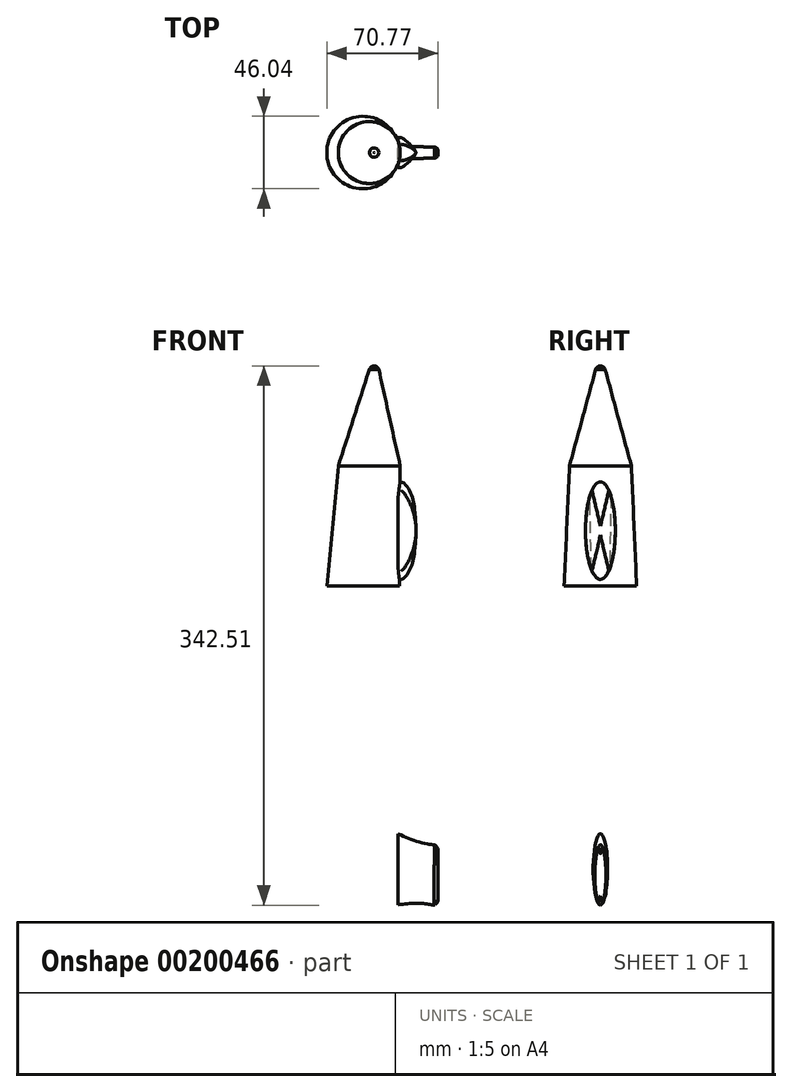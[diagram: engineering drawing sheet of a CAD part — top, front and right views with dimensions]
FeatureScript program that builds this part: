
annotation { "Feature Type Name" : "Feature", "Feature Type Description" : "" }
export const myFeature = defineFeature(function(context is Context, id is Id, definition is map)
    precondition{}
    {
        {
            var Q0;
            Q0=qCreatedBy(makeId("Top.planeOp"),FACE);
            var sketch = newSketch(context, id + "F0", { "sketchPlane" : qUnion([Q0])});
            skCircle(sketch, "E0", {"center": v(0, 0) * mm, "radius": 23.24 * mm});
            skSolve(sketch);
        }
        {
            var Q0;
            Q0=makeQuery(id+"F0.imprint","IMPRINT",FACE,{"disambiguationData":[TD([[makeQuery(id+"F0.imprint","IMPRINT",EDGE,{"derivedFrom":sQuery(id+"F0.wireOp",EDGE,"E0")}),1.0]])]});
            extrude(context, id + "F1", {"entities" : qUnion([Q0]), "depth" : 76.2 * mm, "hasSecondDirection" : true, "secondDirectionOppositeDirection" : true, "secondDirectionDepth" : 127 * mm});
        }
        {
            var Q0;
            Q0=makeQuery(id+"F1.opExtrude","CAP_FACE",FACE,{"disambiguationData":[OSD([sQuery(id+"F0.wireOp",EDGE,"E0")])],"isStart":false});
            var sketch = newSketch(context, id + "F2", { "sketchPlane" : qUnion([Q0])});
            skCircle(sketch, "E1", {"center": v(0, 0) * mm, "radius": 23.02 * mm});
            skSolve(sketch);
        }
        {
            var Q0;
            Q0=makeQuery(id+"F2.imprint","IMPRINT",FACE,{"disambiguationData":[TD([[makeQuery(id+"F2.imprint","IMPRINT",EDGE,{"derivedFrom":sQuery(id+"F2.wireOp",EDGE,"E1")}),1.0]])]});
            cPlane(context, id + "F3", {"entities" : qUnion([Q0]), "cplaneType" : CPlaneType.OFFSET, "offset" : 76.2 * mm, "width" : 152.4 * mm, "height" : 152.4 * mm});
        }
        {
            var Q0;
            Q0=qCreatedBy(id+"F3.planeOp",FACE);
            var sketch = newSketch(context, id + "F4", { "sketchPlane" : qUnion([Q0])});
            skCircle(sketch, "E2", {"center": v(3.96, 0) * mm, "radius": 19.65 * mm});
            skSolve(sketch);
        }
        {
            var Q1;
            Q1=makeQuery(id+"F2.imprint","IMPRINT",FACE,{"disambiguationData":[TD([[makeQuery(id+"F2.imprint","IMPRINT",EDGE,{"derivedFrom":sQuery(id+"F2.wireOp",EDGE,"E1")}),1.0]])]});
            var Q2;
            Q2=makeQuery(id+"F4.imprint","IMPRINT",FACE,{"disambiguationData":[TD([[makeQuery(id+"F4.imprint","IMPRINT",EDGE,{"derivedFrom":sQuery(id+"F4.wireOp",EDGE,"E2")}),1.0]])]});
            loft(context, id + "F5", {"sheetProfilesArray" : [{ "sheetProfileEntities" : qUnion([Q1]) }, { "sheetProfileEntities" : qUnion([Q2]) }]});
        }
        {
            var Q0;
            Q0=qCreatedBy(makeId("Right.planeOp"),FACE);
            cPlane(context, id + "F6", {"entities" : qUnion([Q0]), "cplaneType" : CPlaneType.OFFSET, "offset" : 17.78 * mm, "width" : 152.4 * mm, "height" : 152.4 * mm});
        }
        {
            var Q0;
            Q0=qCreatedBy(makeId("Front.planeOp"),FACE);
            var sketch = newSketch(context, id + "F7", { "sketchPlane" : qUnion([Q0])});
            skEllipse(sketch, "E3", {"center": v(0, 0) * mm, "majorRadius": 116.9 * mm, "minorRadius": 9.43 * mm, "majorAxis": v(0, 1)});
            skSolve(sketch);
        }
        {
            var Q0;
            Q0=qCreatedBy(makeId("Front.planeOp"),FACE);
            cPlane(context, id + "F8", {"entities" : qUnion([Q0]), "cplaneType" : CPlaneType.OFFSET, "offset" : 88.9 * mm, "width" : 152.4 * mm, "height" : 152.4 * mm});
        }
        {
            var Q0;
            Q0=qCreatedBy(id+"F8.planeOp",FACE);
            var sketch = newSketch(context, id + "F9", { "sketchPlane" : qUnion([Q0])});
            skEllipse(sketch, "E4", {"center": v(0, -72.55) * mm, "majorRadius": 42.33 * mm, "minorRadius": 3.66 * mm, "majorAxis": v(0, 1)});
            skSolve(sketch);
        }
        {
            var Q0;
            Q0=makeQuery(id+"F7.imprint","IMPRINT",FACE,{"disambiguationData":[TD([[makeQuery(id+"F7.imprint","IMPRINT",EDGE,{"derivedFrom":sQuery(id+"F7.wireOp",EDGE,"E3")}),1.0]])]});
            var Q1;
            Q1=makeQuery(id+"F9.imprint","IMPRINT",FACE,{"disambiguationData":[TD([[makeQuery(id+"F9.imprint","IMPRINT",EDGE,{"derivedFrom":sQuery(id+"F9.wireOp",EDGE,"E4")}),1.0]])]});
            loft(context, id + "F10", {"bodyType" : ToolBodyType.SURFACE, "wireProfilesArray" : [{ "wireProfileEntities" : qUnion([Q0]) }, { "wireProfileEntities" : qUnion([Q1]) }]});
        }
        {
            var Q0;
            Q0=makeQuery(id+"F10.opLoft","SWEPT_BODY",BODY,{"disambiguationData":[OSD([sQuery(id+"F7.wireOp",EDGE,"E3"),sQuery(id+"F9.wireOp",EDGE,"E4")])]});
            var Q1;
            Q1=qCreatedBy(makeId("Front.planeOp"),FACE);
            mirror(context, id + "F11", {"entities" : qUnion([Q0]), "mirrorPlane" : qUnion([Q1])});
        }
        {
            var Q0;
            Q0=makeQuery(id+"F4.imprint","IMPRINT",FACE,{"disambiguationData":[TD([[makeQuery(id+"F4.imprint","IMPRINT",EDGE,{"derivedFrom":sQuery(id+"F4.wireOp",EDGE,"E2")}),1.0]])]});
            cPlane(context, id + "F12", {"entities" : qUnion([Q0]), "cplaneType" : CPlaneType.OFFSET, "offset" : 63.5 * mm, "width" : 152.4 * mm, "height" : 152.4 * mm});
        }
        {
            var Q0;
            Q0=qCreatedBy(id+"F12.planeOp",FACE);
            var sketch = newSketch(context, id + "F13", { "sketchPlane" : qUnion([Q0])});
            skCircle(sketch, "E5", {"center": v(7.13, 0) * mm, "radius": 2.4 * mm});
            skSolve(sketch);
        }
        {
            var Q0;
            Q0=makeQuery(id+"F13.imprint","IMPRINT",FACE,{"disambiguationData":[TD([[makeQuery(id+"F13.imprint","IMPRINT",EDGE,{"derivedFrom":sQuery(id+"F13.wireOp",EDGE,"E5")}),1.0]])]});
            var Q1;
            Q1=makeQuery(id+"F4.imprint","IMPRINT",FACE,{"disambiguationData":[TD([[makeQuery(id+"F4.imprint","IMPRINT",EDGE,{"derivedFrom":sQuery(id+"F4.wireOp",EDGE,"E2")}),1.0]])]});
            loft(context, id + "F14", {"sheetProfilesArray" : [{ "sheetProfileEntities" : qUnion([Q0]) }, { "sheetProfileEntities" : qUnion([Q1]) }]});
        }
        {
            var Q0;
            Q0=makeQuery(id+"F14.opLoft","CAP_FACE",FACE,{"disambiguationData":[OSD([makeQuery(id+"F13.imprint","IMPRINT",FACE,{"disambiguationData":[TD([[makeQuery(id+"F13.imprint","IMPRINT",EDGE,{"derivedFrom":sQuery(id+"F13.wireOp",EDGE,"E5")}),1.0]])]})])],"isStart":true});
            fillet(context, id + "F15", {"entities" : qUnion([Q0]), "radius" : 3.05 * mm, "tangentPropagation" : true, "allowEdgeOverflow" : false});
        }
        {
            var Q0;
            Q0=qCreatedBy(id+"F6.planeOp",FACE);
            cPlane(context, id + "F16", {"entities" : qUnion([Q0]), "cplaneType" : CPlaneType.OFFSET, "offset" : 4.57 * mm, "width" : 152.4 * mm, "height" : 152.4 * mm});
        }
        {
            var Q0;
            Q0=qCreatedBy(id+"F16.planeOp",FACE);
            var sketch = newSketch(context, id + "F17", { "sketchPlane" : qUnion([Q0])});
            skEllipse(sketch, "E6", {"center": v(0, 111.29) * mm, "majorRadius": 30.95 * mm, "minorRadius": 9.47 * mm, "majorAxis": v(0, 1)});
            skSolve(sketch);
        }
        {
            var Q0;
            Q0=makeQuery(id+"F17.imprint","IMPRINT",FACE,{"disambiguationData":[TD([[makeQuery(id+"F17.imprint","IMPRINT",EDGE,{"derivedFrom":sQuery(id+"F17.wireOp",EDGE,"E6")}),1.0]])]});
            extrude(context, id + "F18", {"entities" : qUnion([Q0]), "operationType" : NewBodyOperationType.ADD, "depth" : 11.18 * mm});
        }
        {
            var Q0;
            Q0=makeQuery(id+"F18.opExtrude","CAP_EDGE",EDGE,{"disambiguationData":[OSD([sQuery(id+"F17.wireOp",EDGE,"E6")])],"isStart":false});
            fillet(context, id + "F19", {"entities" : qUnion([Q0]), "radius" : 9.42 * mm, "tangentPropagation" : true, "rho" : .15, "crossSection" : FilletCrossSection.CONIC, "allowEdgeOverflow" : false});
        }
        {
            var Q0;
            Q0=qCreatedBy(id+"F16.planeOp",FACE);
            var sketch = newSketch(context, id + "F20", { "sketchPlane" : qUnion([Q0])});
            skEllipse(sketch, "E7", {"center": v(0, -103.87) * mm, "majorRadius": 22.62 * mm, "minorRadius": 4.6 * mm, "majorAxis": v(0, 1)});
            skSolve(sketch);
        }
        {
            var Q0;
            Q0=qCreatedBy(id+"F16.planeOp",FACE);
            cPlane(context, id + "F21", {"entities" : qUnion([Q0]), "cplaneType" : CPlaneType.OFFSET, "offset" : 25.4 * mm, "width" : 152.4 * mm, "height" : 152.4 * mm});
        }
        {
            var Q0;
            Q0=qCreatedBy(id+"F21.planeOp",FACE);
            var sketch = newSketch(context, id + "F22", { "sketchPlane" : qUnion([Q0])});
            skEllipse(sketch, "E8", {"center": v(0, -107.9) * mm, "majorRadius": 19.49 * mm, "minorRadius": 3.54 * mm, "majorAxis": v(0, 1)});
            skSolve(sketch);
        }
        {
            var Q0;
            Q0=makeQuery(id+"F22.imprint","IMPRINT",FACE,{"disambiguationData":[TD([[makeQuery(id+"F22.imprint","IMPRINT",EDGE,{"derivedFrom":sQuery(id+"F22.wireOp",EDGE,"E8")}),1.0]])]});
            var Q1;
            Q1=makeQuery(id+"F20.imprint","IMPRINT",FACE,{"disambiguationData":[TD([[makeQuery(id+"F20.imprint","IMPRINT",EDGE,{"derivedFrom":sQuery(id+"F20.wireOp",EDGE,"E7")}),1.0]])]});
            loft(context, id + "F23", {"sheetProfilesArray" : [{ "sheetProfileEntities" : qUnion([Q0]) }, { "sheetProfileEntities" : qUnion([Q1]) }]});
        }
        {
            var Q0;
            Q0=makeQuery(id+"F23.opLoft","MID_CAP_EDGE",EDGE,{"disambiguationData":[OSD([sQuery(id+"F22.wireOp",EDGE,"E8")])],"capPos":0.0});
            fillet(context, id + "F24", {"entities" : qUnion([Q0]), "radius" : 2.54 * mm, "tangentPropagation" : true, "allowEdgeOverflow" : false});
        }
        {
            var Q0;
            Q0=makeQuery(id+"F1.opExtrude","CAP_FACE",FACE,{"disambiguationData":[OSD([sQuery(id+"F0.wireOp",EDGE,"E0")])],"isStart":true});
            var sketch = newSketch(context, id + "F25", { "sketchPlane" : qUnion([Q0])});
            skCircle(sketch, "E9", {"center": v(0, 0) * mm, "radius": 23.2 * mm});
            skSolve(sketch);
        }
        {
            var Q0;
            Q0=sQuery(id+"F25.wireOp",VERTEX,"E9.center");
            var Q1;
            Q1=makeQuery(id+"F1.opExtrude","SWEPT_BODY",BODY,{"disambiguationData":[OSD([sQuery(id+"F0.wireOp",EDGE,"E0")])]});
            hole(context, id + "F26", {"style" : HoleStyle.SIMPLE, "endStyle" : HoleEndStyle.THROUGH, "holeDiameter" : 2616.2 * mm, "locations" : qUnion([Q0]), "scope" : qUnion([Q1]), "isTappedThrough" : true});
        }
    });
